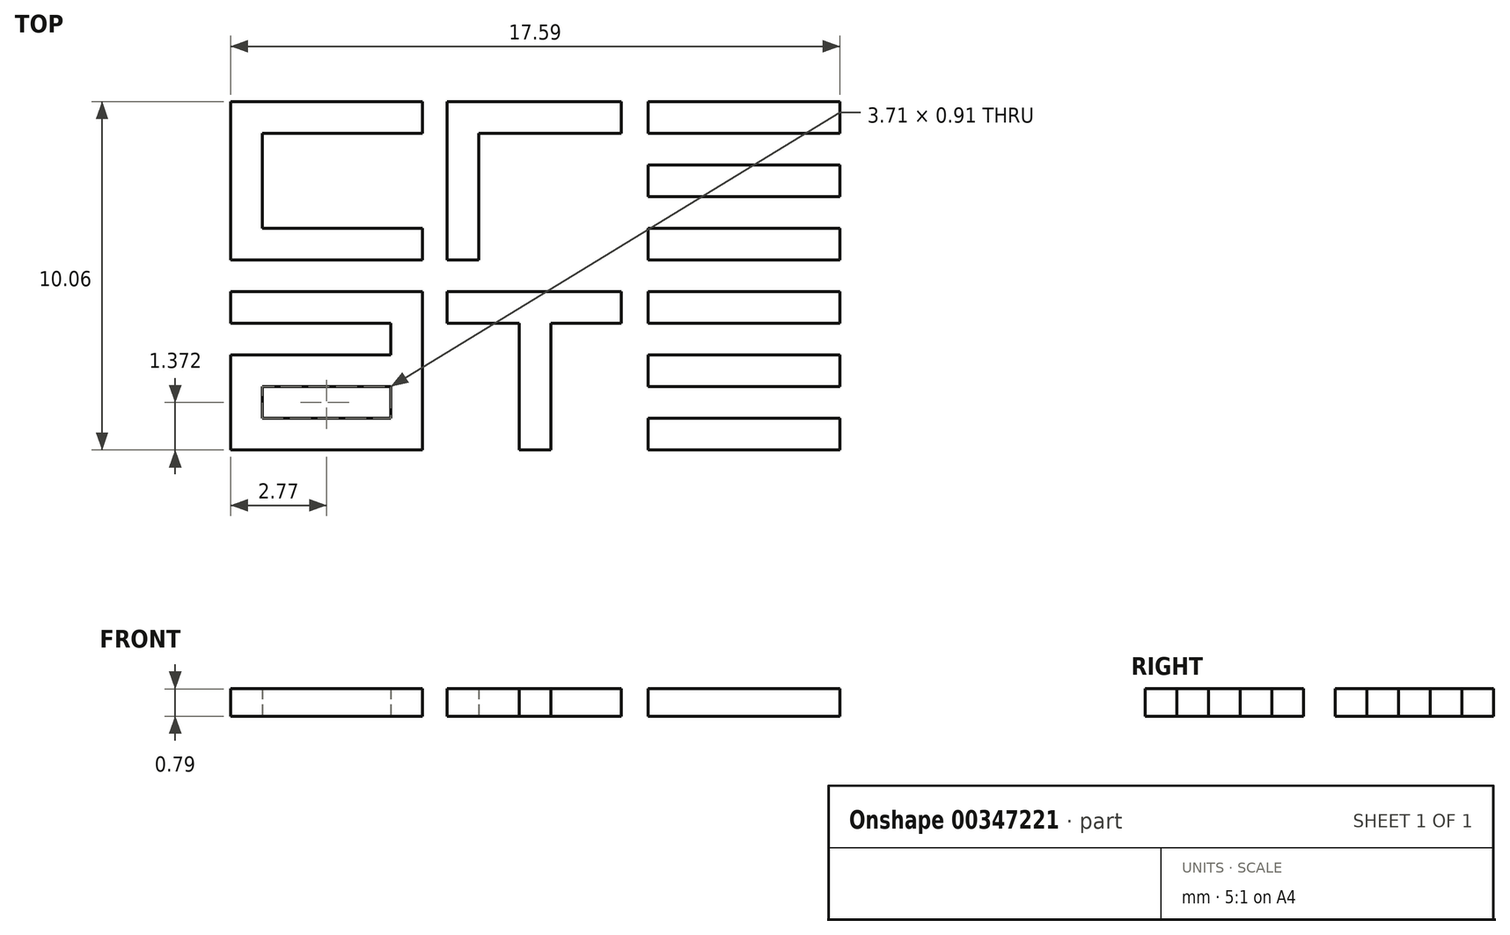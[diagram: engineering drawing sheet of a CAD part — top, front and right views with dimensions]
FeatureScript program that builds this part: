
annotation { "Feature Type Name" : "Feature", "Feature Type Description" : "" }
export const myFeature = defineFeature(function(context is Context, id is Id, definition is map)
    precondition{}
    {
        {
            var Q0;
            Q0=qCreatedBy(makeId("Top.planeOp"),FACE);
            var sketch = newSketch(context, id + "F0", { "sketchPlane" : qUnion([Q0])});
            skLineSegment(sketch, "E0.bottom", {"start": v(19.05, 19.05) * mm, "end": v(-19.05, 19.05) * mm});
            skLineSegment(sketch, "E0.top", {"start": v(19.05, -19.05) * mm, "end": v(-19.05, -19.05) * mm});
            skLineSegment(sketch, "E0.left", {"start": v(19.05, 19.05) * mm, "end": v(19.05, -19.05) * mm});
            skLineSegment(sketch, "E0.right", {"start": v(-19.05, 19.05) * mm, "end": v(-19.05, -19.05) * mm});
            skPoint(sketch, "E0.middle", {"position": v(0, 0) * mm});
            skLineSegment(sketch, "E1.bottom", {"start": v(-8.79, 5.02) * mm, "end": v(8.8, 5.02) * mm});
            skLineSegment(sketch, "E1.top", {"start": v(-8.79, -5.04) * mm, "end": v(8.8, -5.04) * mm});
            skLineSegment(sketch, "E1.left", {"start": v(-8.79, 5.02) * mm, "end": v(-8.79, -5.04) * mm});
            skLineSegment(sketch, "E1.right", {"start": v(8.8, 5.02) * mm, "end": v(8.8, -5.04) * mm});
            skLineSegment(sketch, "E2", {"start": v(-8.79, 0.45) * mm, "end": v(-3.25, 0.45) * mm});
            skLineSegment(sketch, "E3", {"start": v(-3.25, 0.45) * mm, "end": v(-3.25, 1.36) * mm});
            skLineSegment(sketch, "E4", {"start": v(-3.25, 1.36) * mm, "end": v(-7.87, 1.36) * mm});
            skLineSegment(sketch, "E5", {"start": v(-3.25, 2.73) * mm, "end": v(-4.32, 2.73) * mm, "construction": true});
            skLineSegment(sketch, "E6.MirrorCS", {"start": v(-3.25, 4.1) * mm, "end": v(-7.87, 4.1) * mm});
            skLineSegment(sketch, "E7", {"start": v(-7.87, 4.1) * mm, "end": v(-7.87, 1.36) * mm});
            skLineSegment(sketch, "E8", {"start": v(-2.54, 0.45) * mm, "end": v(-2.54, 5.02) * mm});
            skLineSegment(sketch, "E9", {"start": v(-2.54, 0.45) * mm, "end": v(-1.62, 0.45) * mm});
            skLineSegment(sketch, "E10.trimOffspring", {"start": v(-3.25, 4.1) * mm, "end": v(-3.25, 5.02) * mm});
            skLineSegment(sketch, "E11", {"start": v(-1.62, 4.1) * mm, "end": v(-1.62, 0.45) * mm});
            skLineSegment(sketch, "E12", {"start": v(8.8, 0.45) * mm, "end": v(3.26, 0.45) * mm});
            skLineSegment(sketch, "E13.0", {"start": v(8.8, 1.36) * mm, "end": v(3.27, 1.36) * mm});
            skLineSegment(sketch, "E14.0", {"start": v(8.8, 2.28) * mm, "end": v(3.26, 2.28) * mm});
            skLineSegment(sketch, "E15.0", {"start": v(8.8, 3.2) * mm, "end": v(3.27, 3.2) * mm});
            skLineSegment(sketch, "E16.0", {"start": v(8.8, 4.1) * mm, "end": v(3.26, 4.1) * mm});
            skLineSegment(sketch, "E17", {"start": v(3.26, 0.45) * mm, "end": v(3.27, 1.36) * mm});
            skLineSegment(sketch, "E18", {"start": v(3.26, 2.28) * mm, "end": v(3.27, 3.2) * mm});
            skLineSegment(sketch, "E19", {"start": v(3.26, 4.1) * mm, "end": v(3.26, 5.02) * mm});
            skLineSegment(sketch, "E20", {"start": v(-1.62, 4.1) * mm, "end": v(2.5, 4.1) * mm});
            skLineSegment(sketch, "E21", {"start": v(2.5, 4.1) * mm, "end": v(2.5, 5.02) * mm});
            skLineSegment(sketch, "E22", {"start": v(-8.79, -0.47) * mm, "end": v(8.8, -0.47) * mm});
            skLineSegment(sketch, "E23", {"start": v(3.26, -0.47) * mm, "end": v(3.26, -5.04) * mm});
            skLineSegment(sketch, "E24.0", {"start": v(-7.87, -4.13) * mm, "end": v(-0.46, -4.13) * mm});
            skLineSegment(sketch, "E25.0", {"start": v(-7.87, -3.21) * mm, "end": v(-4.17, -3.21) * mm});
            skLineSegment(sketch, "E26.0", {"start": v(-8.79, -2.3) * mm, "end": v(-0.46, -2.3) * mm});
            skLineSegment(sketch, "E27.0", {"start": v(-8.79, -1.38) * mm, "end": v(-4.17, -1.38) * mm});
            skLineSegment(sketch, "E28", {"start": v(2.5, -0.47) * mm, "end": v(2.5, -1.38) * mm});
            skLineSegment(sketch, "E29", {"start": v(-2.54, -0.47) * mm, "end": v(-2.54, -1.38) * mm});
            skLineSegment(sketch, "E30", {"start": v(-0.46, -1.38) * mm, "end": v(-0.46, -5.04) * mm});
            skLineSegment(sketch, "E31.0", {"start": v(0.45, -1.38) * mm, "end": v(0.45, -5.04) * mm});
            skLineSegment(sketch, "E32.trimOffspring", {"start": v(0.45, -1.38) * mm, "end": v(8.8, -1.38) * mm});
            skLineSegment(sketch, "E33.trimOffspring", {"start": v(0.45, -2.3) * mm, "end": v(8.8, -2.3) * mm});
            skLineSegment(sketch, "E34.trimOffspring", {"start": v(0.45, -4.13) * mm, "end": v(8.8, -4.13) * mm});
            skLineSegment(sketch, "E35", {"start": v(-3.25, -0.47) * mm, "end": v(-3.25, -5.04) * mm});
            skLineSegment(sketch, "E36", {"start": v(-4.17, -1.38) * mm, "end": v(-4.17, -2.3) * mm});
            skLineSegment(sketch, "E37", {"start": v(-4.17, -3.21) * mm, "end": v(-4.17, -4.13) * mm});
            skLineSegment(sketch, "E38", {"start": v(-7.87, -3.21) * mm, "end": v(-7.87, -4.13) * mm});
            skLineSegment(sketch, "E39.trimOffspring", {"start": v(-3.25, -1.38) * mm, "end": v(-0.46, -1.38) * mm});
            skLineSegment(sketch, "E40.trimOffspring", {"start": v(-3.25, -3.21) * mm, "end": v(8.8, -3.21) * mm});
            skSolve(sketch);
        }
        {
            var Q0;
            {var subQ0=sQuery(id+"F0.wireOp",EDGE,"E2");Q0=makeQuery(id+"F0.imprint","IMPRINT",FACE,{"disambiguationData":[TD([[makeQuery(id+"F0.imprint","IMPRINT",EDGE,{"derivedFrom":subQ0}),1.0]])]});}
            var Q1;
            {var subQ0=sQuery(id+"F0.wireOp",EDGE,"E8");Q1=makeQuery(id+"F0.imprint","IMPRINT",FACE,{"disambiguationData":[TD([[makeQuery(id+"F0.imprint","IMPRINT",EDGE,{"derivedFrom":subQ0}),-1.0]])]});}
            var Q2;
            {var subQ3=sQuery(id+"F0.wireOp",EDGE,"E19");Q2=makeQuery(id+"F0.imprint","IMPRINT",FACE,{"disambiguationData":[TD([[makeQuery(id+"F0.imprint","IMPRINT",EDGE,{"derivedFrom":subQ3}),-1.0]])]});}
            var Q3;
            {var subQ5=sQuery(id+"F0.wireOp",EDGE,"E18");Q3=makeQuery(id+"F0.imprint","IMPRINT",FACE,{"disambiguationData":[TD([[makeQuery(id+"F0.imprint","IMPRINT",EDGE,{"derivedFrom":subQ5}),-1.0]])]});}
            var Q4;
            {var subQ0=sQuery(id+"F0.wireOp",EDGE,"E12");Q4=makeQuery(id+"F0.imprint","IMPRINT",FACE,{"disambiguationData":[TD([[makeQuery(id+"F0.imprint","IMPRINT",EDGE,{"derivedFrom":subQ0}),-1.0]])]});}
            var Q5;
            {var subQ0=sQuery(id+"F0.wireOp",EDGE,"E22");var subQ1=sQuery(id+"F0.wireOp",EDGE,"E1.right");var subQ2=makeQuery(id+"F0.imprint","INTERSECT",VERTEX,{"derivedFrom":[subQ1,subQ0]});Q5=makeQuery(id+"F0.imprint","IMPRINT",FACE,{"disambiguationData":[TD([[makeQuery(id+"F0.imprint","IMPRINT",EDGE,{"disambiguationData":[TD([[subQ2,-1.0]])],"derivedFrom":subQ1}),-1.0]])]});}
            var Q6;
            {var subQ0=sQuery(id+"F0.wireOp",EDGE,"E33.trimOffspring");var subQ1=sQuery(id+"F0.wireOp",EDGE,"E1.right");var subQ2=makeQuery(id+"F0.imprint","INTERSECT",VERTEX,{"derivedFrom":[subQ1,subQ0]});Q6=makeQuery(id+"F0.imprint","IMPRINT",FACE,{"disambiguationData":[TD([[makeQuery(id+"F0.imprint","IMPRINT",EDGE,{"disambiguationData":[TD([[subQ2,-1.0]])],"derivedFrom":subQ1}),-1.0]])]});}
            var Q7;
            {var subQ0=sQuery(id+"F0.wireOp",EDGE,"E1.right");var subQ1=sQuery(id+"F0.wireOp",EDGE,"E1.top");var subQ2=makeQuery(id+"F0.imprint","INTERSECT",VERTEX,{"derivedFrom":[subQ1,subQ0]});Q7=makeQuery(id+"F0.imprint","IMPRINT",FACE,{"disambiguationData":[TD([[makeQuery(id+"F0.imprint","IMPRINT",EDGE,{"disambiguationData":[TD([[subQ2,1.0]])],"derivedFrom":subQ1}),1.0]])]});}
            var Q8;
            {var subQ5=sQuery(id+"F0.wireOp",EDGE,"E28");Q8=makeQuery(id+"F0.imprint","IMPRINT",FACE,{"disambiguationData":[TD([[makeQuery(id+"F0.imprint","IMPRINT",EDGE,{"derivedFrom":subQ5}),-1.0]])]});}
            var Q9;
            {var subQ4=sQuery(id+"F0.wireOp",EDGE,"E30");var subQ7=sQuery(id+"F0.wireOp",EDGE,"E1.top");var subQ8=makeQuery(id+"F0.imprint","INTERSECT",VERTEX,{"derivedFrom":[subQ7,subQ4]});Q9=makeQuery(id+"F0.imprint","IMPRINT",FACE,{"disambiguationData":[TD([[makeQuery(id+"F0.imprint","IMPRINT",EDGE,{"disambiguationData":[TD([[subQ8,-1.0]])],"derivedFrom":subQ7}),1.0]])]});}
            var Q10;
            Q10=makeQuery(id+"F0.imprint","IMPRINT",FACE,{"disambiguationData":[TD([[makeQuery(id+"F0.imprint","IMPRINT",EDGE,{"derivedFrom":sQuery(id+"F0.wireOp",EDGE,"E25.0")}),1.0]])]});
            var Q11;
            {var subQ0=sQuery(id+"F0.wireOp",EDGE,"E27.0");Q11=makeQuery(id+"F0.imprint","IMPRINT",FACE,{"disambiguationData":[TD([[makeQuery(id+"F0.imprint","IMPRINT",EDGE,{"derivedFrom":subQ0}),1.0]])]});}
            extrude(context, id + "F1", {"entities" : qUnion([Q0, Q1, Q2, Q3, Q4, Q5, Q6, Q7, Q8, Q9, Q10, Q11]), "depth" : 0.8 * mm});
        }
    });
